# Revit family: ЗК РАШВОРК арт.103
name_source: partatom
category: Арматура трубопроводов
units: mm (PartAtom-declared; Revit-internal decimal feet)

## family parameters
Всегда вертикально = Да
На основе рабочей плоскости = Нет
Общий = Нет
При загрузке вырезать с полостями = Нет
Размер круглого соединителя = Использовать диаметр
Тип детали = Нормальный

## types (19) — shared parameters
ADSK_Завод-изготовитель = ООО ТД "РАШВОРК"
H2 = 60 мм
URL = https://rwru.ru
Корпус = GGG40
zero-valued in all types: Отметка по умолчанию

## per-type parameters (varying)
| type | ADSK_Единица измерения | ADSK_Масса | ADSK_Наименование краткое | B | D | D(ISO) | D1 | DN | DN(D) | DNсоединителя | G | H | H1 | H11 | HH | L | L1 | L2 | V1 | f | Высота | Длина |
| Задвижка с обрезиненным клином РАШВОРК 103-040-16, DN040, PN16, корпус GGG50, клин - GGG50, уплотнение - EPDM, Ф/Ф, ISO5211, F10, с голым штоком | ШТ | 10 | 103-040-16 | 19 мм | 150 мм | 125 мм | 30 мм | 40 мм | 20 мм | 40 мм | 84 мм | 200 мм | 163 мм | 105 мм | 20 мм | 140 мм | 100 мм | 50 мм | 112 мм | 3 мм | 70 мм | 342 мм |
| Задвижка с обрезиненным клином РАШВОРК 103-050-16, DN050, PN16, корпус GGG50, клин - GGG50, уплотнение - EPDM, Ф/Ф, ISO5211, F10, с голым штоком | шт | 10.5 | 103-050-16 | 19 мм | 165 мм | 125 мм | 35 мм | 50 мм | 20 мм | 50 мм | 99 мм | 207 мм | 170 мм | 110 мм | 20 мм | 150 мм | 100 мм | 50 мм | 126 мм | 3 мм | 75 мм | 400 мм |
| Задвижка с обрезиненным клином РАШВОРК 103-065-16, DN065, PN16, корпус GGG50, клин - GGG50, уплотнение - EPDM, Ф/Ф, ISO5211, F10, с голым штоком | шт | 13.5 | 103-065-16 | 19 мм | 185 мм | 125 мм | 45 мм | 65 мм | 20 мм | 65 мм | 118 мм | 233 мм | 206 мм | 150 мм | 20 мм | 170 мм | 105 мм | 50 мм | 112 мм | 3 мм | 85 мм | 342 мм |
| Задвижка с обрезиненным клином РАШВОРК 103-080-16, DN080, PN16, корпус GGG50, клин - GGG50, уплотнение - EPDM, Ф/Ф, ISO5211, F10, с голым штоком | шт | 16 | 103-080-16 | 19 мм | 200 мм | 125 мм | 52 мм | 80 мм | 20 мм | 80 мм | 132 мм | 257 мм | 220 мм | 160 мм | 20 мм | 180 мм | 125 мм | 50 мм | 160 мм | 3 мм | 90 мм | 342 мм |
| Задвижка с обрезиненным клином РАШВОРК 103-100-16, DN100, PN16, корпус GGG50, клин - GGG50, уплотнение - EPDM, Ф/Ф, ISO5211, F10, с голым штоком | шт | 19.2 | 103-100-16 | 19 мм | 220 мм | 125 мм | 60 мм | 100 мм | 20 мм | 100 мм | 156 мм | 288 мм | 251 мм | 165 мм | 20 мм | 190 мм | 120 мм | 50 мм | 180 мм | 3 мм | 95 мм | 342 мм |
| Задвижка с обрезиненным клином РАШВОРК 103-125-16, DN125, PN16, корпус GGG50, клин - GGG50, уплотнение - EPDM, Ф/Ф, ISO5211, F10, с голым штоком | шт | 26.5 | 103-125-16 | 19 мм | 250 мм | 125 мм | 80 мм | 125 мм | 20 мм | 125 мм | 184 мм | 331 мм | 294 мм | 215 мм | 20 мм | 200 мм | 130 мм | 50 мм | 230 мм | 3 мм | 100 мм | 342 мм |
| Задвижка с обрезиненным клином РАШВОРК 103-150-16, DN150, PN16, корпус GGG50, клин - GGG50, уплотнение - EPDM, Ф/Ф, ISO5211, F10, с голым штоком | шт | 32.2 | 103-150-16 | 19 мм | 285 мм | 125 мм | 90 мм | 150 мм | 20 мм | 150 мм | 211 мм | 368 мм | 331 мм | 255 мм | 20 мм | 210 мм | 130 мм | 16 мм | 260 мм | 3 мм | 105 мм | 342 мм |
| Задвижка с обрезиненным клином РАШВОРК 103-200-16, DN200, PN16, корпус GGG50, клин - GGG50, уплотнение - EPDM, Ф/Ф, ISO5211, F14, с голым штоком | шт | 55 | 103-200-16 | 20 мм | 340 мм | 175 мм | 110 мм | 200 мм | 30 мм | 200 мм | 266 мм | 469 мм | 408 мм | 340 мм | 22 мм | 230 мм | 150 мм | 100 мм | 310 мм | 3 мм | 115 мм | 342 мм |
| Задвижка с обрезиненным клином РАШВОРК 103-250-16, DN250, PN16, корпус GGG50, клин - GGG50, уплотнение - EPDM, Ф/Ф, ISO5211, F14, с голым штоком | шт | 80 | 103-250-16 | 22 мм | 405 мм | 175 мм | 125 мм | 250 мм | 30 мм | 250 мм | 319 мм | 558 мм | 497 мм | 390 мм | 22 мм | 250 мм | 170 мм | 70 мм | 370 мм | 3 мм | 125 мм | 342 мм |
| Задвижка с обрезиненным клином РАШВОРК 103-300-16, DN300, PN16, корпус GGG50, клин - GGG50, уплотнение - EPDM, Ф/Ф, ISO5211, F14, с голым штоком | шт | 111 | 103-300-16 | 25 мм | 460 мм | 175 мм | 164 мм | 300 мм | 30 мм | 300 мм | 370 мм | 645 мм | 584 мм | 475 мм | 22 мм | 270 мм | 170 мм | 70 мм | 410 мм | 4 мм | 135 мм | 342 мм |
| Задвижка с обрезиненным клином РАШВОРК 103-350-16, DN350, PN16, корпус GGG50, клин - GGG50, уплотнение - EPDM, Ф/Ф, ISO5211, F14, с голым штоком | шт | 228 | 103-350-16 | 27 мм | 520 мм | 175 мм | 198 мм | 350 мм | 36 мм | 350 мм | 429 мм | 830 мм | 775 мм | 645 мм | 22 мм | 290 мм | 210 мм | 70 мм | 530 мм | 4 мм | 145 мм | 342 мм |
| Задвижка с обрезиненным клином РАШВОРК 103-400-16, DN400, PN16, корпус GGG50, клин - GGG50, уплотнение - EPDM, Ф/Ф, ISO5211, F14, с голым штоком | шт | 257 | 103-400-16 | 28 мм | 580 мм | 175 мм | 220 мм | 400 мм | 36 мм | 400 мм | 480 мм | 897 мм | 842 мм | 692 мм | 22 мм | 310 мм | 210 мм | 100 мм | 595 мм | 4 мм | 155 мм | 342 мм |
| Задвижка с обрезиненным клином РАШВОРК 103-450-16, DN450, PN16, корпус GGG50, клин - GGG50, уплотнение - EPDM, Ф/Ф, ISO5211, F14, с голым штоком | шт | 326 | 103-450-16 | 30 мм | 640 мм | 175 мм | 235 мм | 450 мм | 36 мм | 450 мм | 548 мм | 965 мм | 910 мм | 735 мм | 22 мм | 330 мм | 220 мм | 100 мм | 630 мм | 4 мм | 165 мм | 342 мм |
| Задвижка с обрезиненным клином РАШВОРК 103-500-16, DN500, PN16, корпус GGG50, клин - GGG50, уплотнение - EPDM, Ф/Ф, ISO5211, F16, с голым штоком | шт | 378 | 103-500-16 | 32 мм | 715 мм | 210 мм | 275 мм | 500 мм | 40 мм | 500 мм | 609 мм | 1084 мм | 1024 мм | 920 мм | 26 мм | 350 мм | 284 мм | 130 мм | 700 мм | 4 мм | 175 мм | 342 мм |
| Задвижка с обрезиненным клином РАШВОРК 103-600-16, DN600, PN16, корпус GGG50, клин - GGG50, уплотнение - EPDM, Ф/Ф, ISO5211, F16, с голым штоком | шт | 650 | 103-600-16 | 36 мм | 840 мм | 210 мм | 300 мм | 600 мм | 40 мм | 600 мм | 720 мм | 1237 мм | 1177 мм | 1052 мм | 26 мм | 390 мм | 312 мм | 130 мм | 775 мм | 5 мм | 195 мм | 342 мм |
| Задвижка с обрезиненным клином РАШВОРК 103-700-16, DN700, PN16, корпус GGG50, клин - GGG50, уплотнение - EPDM, Ф/Ф, ISO5211, с голым штоком | шт | 820.4 | 103-700-16 | 40 мм | 910 мм | 300 мм | 375 мм | 700 мм | 60 мм | 700 мм | 794 мм | 1532 мм | 1468 мм | 1300 мм | 25 мм | 430 мм | 295 мм | 200 мм | 970 мм | 5 мм | 215 мм | 342 мм |
| Задвижка с обрезиненным клином РАШВОРК 103-800-16, DN800, PN16, корпус GGG50, клин - GGG50, уплотнение - EPDM, Ф/Ф, ISO5211, с голым штоком | шт | 1130.4 | 103-800-16 | 43 мм | 1025 мм | 300 мм | 428 мм | 800 мм | 65 мм | 800 мм | 901 мм | 1705 мм | 1640 мм | 1465 мм | 25 мм | 470 мм | 330 мм | 200 мм | 1100 мм | 5 мм | 235 мм | 342 мм |
| Задвижка с обрезиненным клином РАШВОРК 103-900-16, DN900, PN16, корпус GGG50, клин - GGG50, уплотнение - EPDM, Ф/Ф, ISO5211, с голым штоком | шт | 1580.4 | 103-900-16 | 47 мм | 1125 мм | 300 мм | 460 мм | 900 мм | 70 мм | 900 мм | 1001 мм | 1800 мм | 1735 мм | 1580 мм | 25 мм | 510 мм | 358 мм | 200 мм | 1180 мм | 5 мм | 255 мм | 342 мм |
| Задвижка с обрезиненным клином РАШВОРК 103-1000-16, DN1000, PN16, корпус GGG50, клин - GGG50, уплотнение - EPDM, Ф/Ф, ISO5211, с голым штоком | шт | 2980.4 | 103-1000-16 | 50 мм | 1255 мм | 300 мм | 500 мм | 1000 мм | 75 мм | 1000 мм | 1112 мм | 1918 мм | 1853 мм | 1684 мм | 25 мм | 550 мм | 385 мм | 200 мм | 1260 мм | 5 мм | 275 мм | 342 мм |

note: column(s) folded — value = type name in every type: ADSK_Наименование

## geometry (parser evidence)
native form markers: Blend x4
no freeform markers — native parametric forms only
